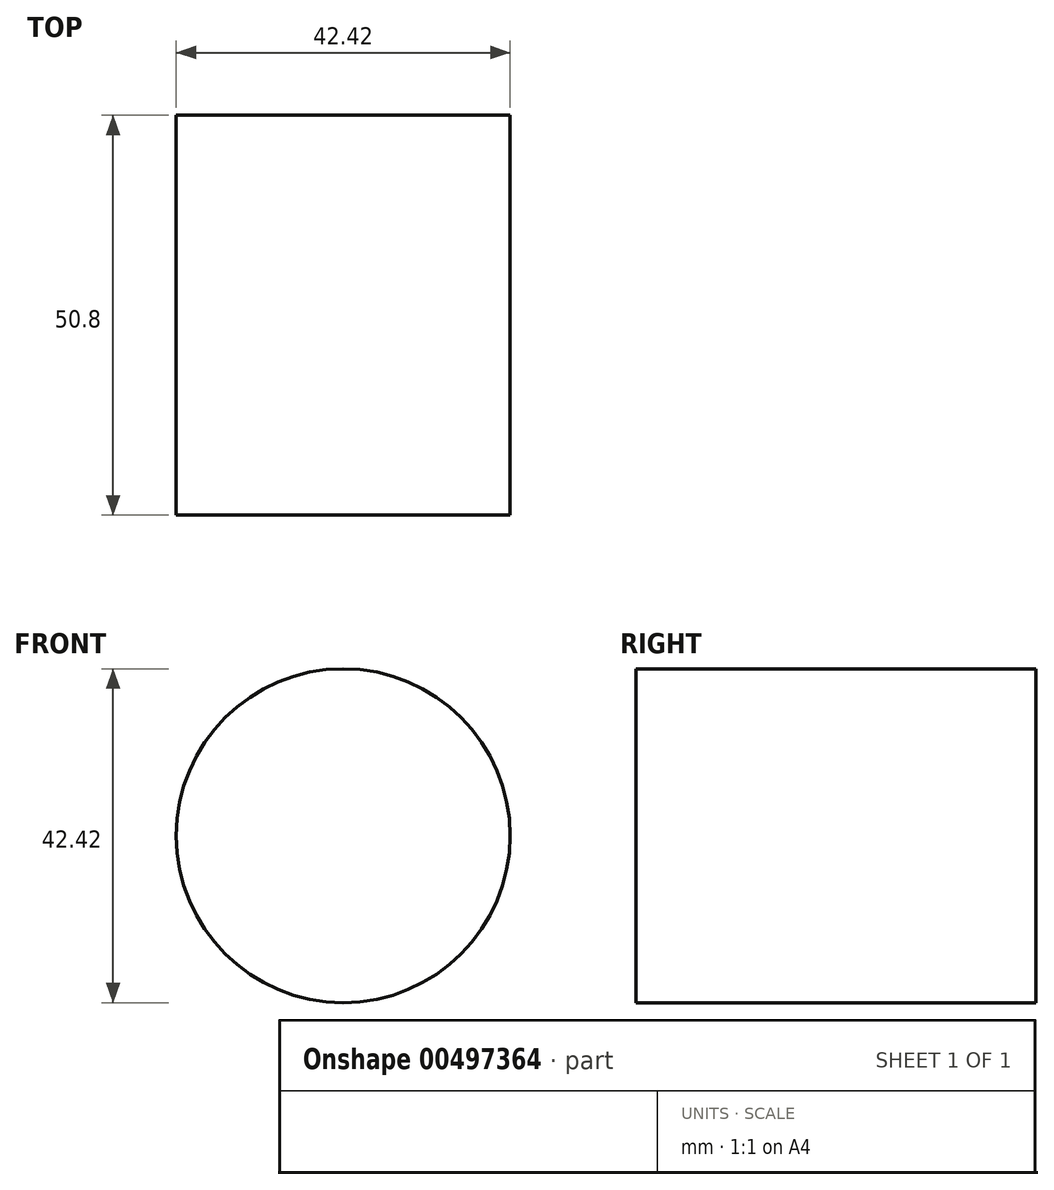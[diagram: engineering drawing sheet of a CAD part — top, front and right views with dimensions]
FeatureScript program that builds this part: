
annotation { "Feature Type Name" : "Feature", "Feature Type Description" : "" }
export const myFeature = defineFeature(function(context is Context, id is Id, definition is map)
    precondition{}
    {
        {
            var Q0;
            Q0=qCreatedBy(makeId("Front.planeOp"),FACE);
            var sketch = newSketch(context, id + "F0", { "sketchPlane" : qUnion([Q0])});
            skCircle(sketch, "E0", {"center": v(-14.14, 12.63) * mm, "radius": 21.2 * mm});
            skSolve(sketch);
        }
        {
            var Q0;
            Q0 = qSketchRegion(id + "F0", true);
            extrude(context, id + "F1", {"entities" : qUnion([Q0]), "depth" : 50.8 * mm});
        }
    });
